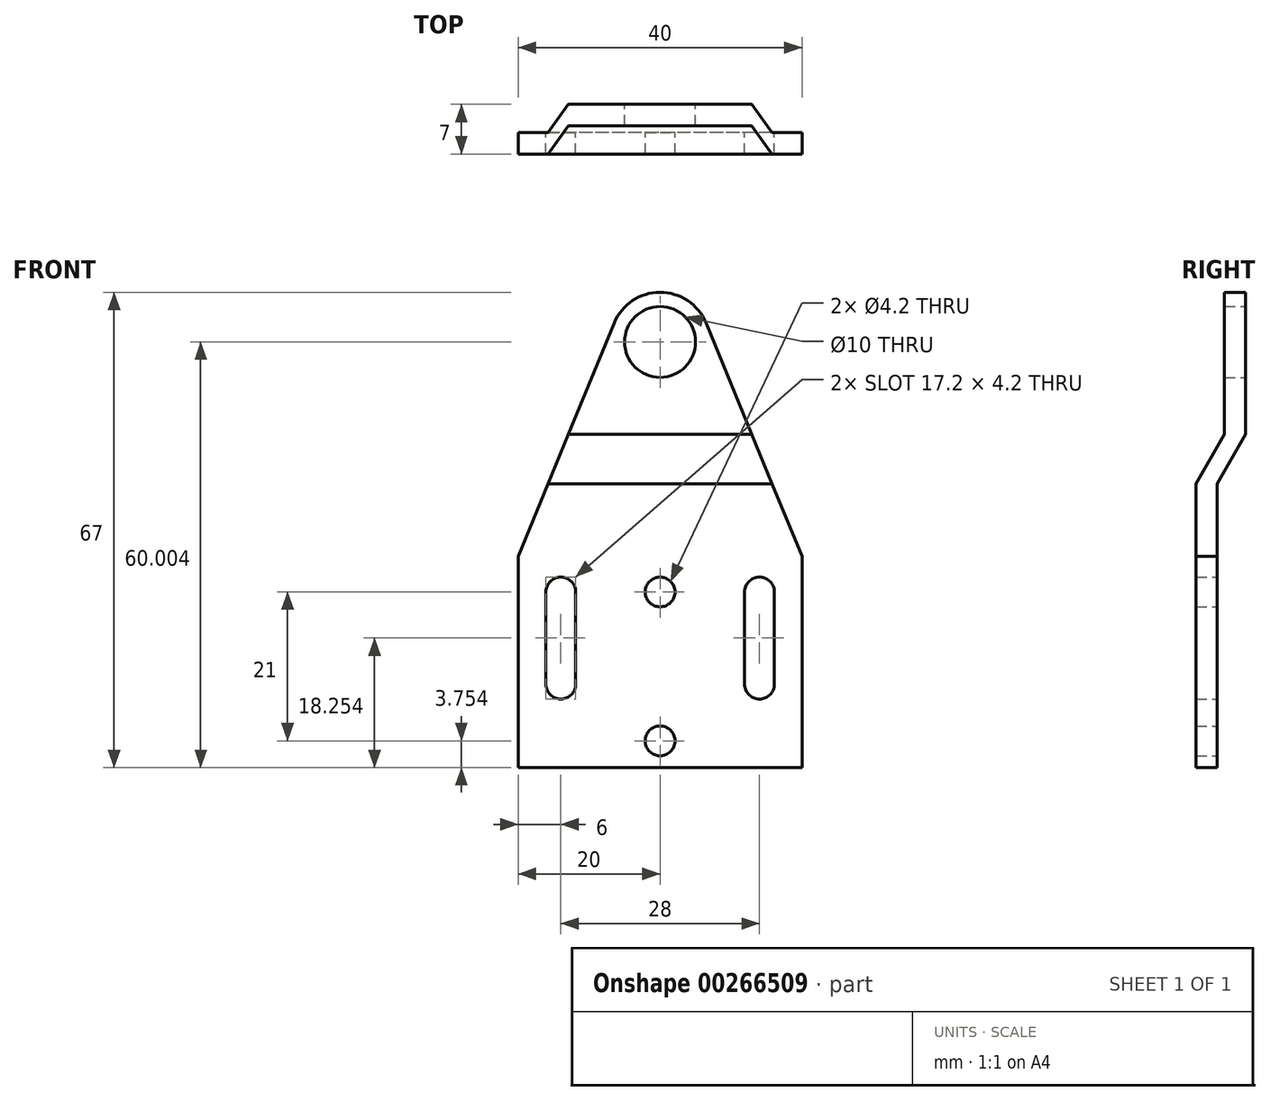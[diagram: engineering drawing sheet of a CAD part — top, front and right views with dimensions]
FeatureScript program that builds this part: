
annotation { "Feature Type Name" : "Feature", "Feature Type Description" : "" }
export const myFeature = defineFeature(function(context is Context, id is Id, definition is map)
    precondition{}
    {
        {
            var Q0;
            Q0=qCreatedBy(makeId("Right.planeOp"),FACE);
            var sketch = newSketch(context, id + "F0", { "sketchPlane" : qUnion([Q0])});
            skLineSegment(sketch, "E0", {"start": v(58.43, 41.65) * mm, "end": v(58.43, 32.15) * mm});
            skLineSegment(sketch, "E1", {"start": v(53.43, 32.15) * mm, "end": v(53.43, 41.65) * mm});
            skArc(sketch, "E2", {"start": v(58.43, 41.65) * mm, "mid": v(55.93, 44.15) * mm, "end": v(53.43, 41.65) * mm});
            skLineSegment(sketch, "E3", {"start": v(77.82, 32.15) * mm, "end": v(39.82, 32.15) * mm, "construction": true});
            skPoint(sketch, "E4.orphan", {"position": v(58.43, 32.15) * mm});
            skLineSegment(sketch, "E5", {"start": v(58.43, 32.15) * mm, "end": v(53.43, 32.15) * mm});
            skSolve(sketch);
        }
        {
            var Q0;
            Q0=makeQuery(id+"F0.imprint","IMPRINT",FACE,{"disambiguationData":[TD([[makeQuery(id+"F0.imprint","IMPRINT",EDGE,{"derivedFrom":sQuery(id+"F0.wireOp",EDGE,"E0")}),-1.0]])]});
            var Q1;
            Q1=sQuery(id+"F0.wireOp",EDGE,"E3");
            revolve(context, id + "F1", {"entities" : qUnion([Q0]), "axis" : qUnion([Q1]), "revolveType" : RevolveType.FULL});
        }
        {
            var Q0;
            Q0=makeQuery(id+"F1.opRevolve","SWEPT_FACE",FACE,{"disambiguationData":[OSD([sQuery(id+"F0.wireOp",EDGE,"E1")])]});
            var sketch = newSketch(context, id + "F2", { "sketchPlane" : qUnion([Q0])});
            skCircle(sketch, "E6", {"center": v(0, 32.15) * mm, "radius": 5 * mm});
            skSolve(sketch);
        }
        {
            var Q0;
            Q0=makeQuery(id+"F2.imprint","IMPRINT",FACE,{"disambiguationData":[TD([[makeQuery(id+"F2.imprint","IMPRINT",EDGE,{"derivedFrom":sQuery(id+"F2.wireOp",EDGE,"E6")}),1.0]])]});
            var Q1;
            Q1=sQuery(id+"F2.wireOp",EDGE,"E6");
            extrude(context, id + "F3", {"entities" : qUnion([Q0]), "operationType" : NewBodyOperationType.ADD, "surfaceEntities" : qUnion([Q1]), "depth" : 10 * mm});
        }
        {
            var Q0;
            Q0=makeQuery(id+"F3.opExtrude","CAP_FACE",FACE,{"disambiguationData":[OSD([sQuery(id+"F2.wireOp",EDGE,"E6")])],"isStart":false});
            var sketch = newSketch(context, id + "F4", { "sketchPlane" : qUnion([Q0])});
            skLineSegment(sketch, "E7", {"start": v(0, 32.15) * mm, "end": v(0, -27.85) * mm, "construction": true});
            skPoint(sketch, "E8", {"position": v(-20, 1.9) * mm});
            skArc(sketch, "E9", {"start": v(6.47, 34.81) * mm, "mid": v(0, 39.15) * mm, "end": v(-6.47, 34.81) * mm});
            skLineSegment(sketch, "E10", {"start": v(-20, 1.9) * mm, "end": v(-6.47, 34.81) * mm});
            skLineSegment(sketch, "E11.MirrorCS", {"start": v(20, 1.9) * mm, "end": v(6.47, 34.81) * mm});
            skLineSegment(sketch, "E12", {"start": v(-20, 1.9) * mm, "end": v(-20, -27.85) * mm});
            skLineSegment(sketch, "E13", {"start": v(-20, -27.85) * mm, "end": v(20, -27.85) * mm});
            skLineSegment(sketch, "E14", {"start": v(20, -27.85) * mm, "end": v(20, 1.9) * mm});
            skArc(sketch, "E15", {"start": v(-11.9, -3.1) * mm, "mid": v(-14, -1) * mm, "end": v(-16.1, -3.1) * mm});
            skArc(sketch, "E16", {"start": v(11.9, -16.1) * mm, "mid": v(14, -18.2) * mm, "end": v(16.1, -16.1) * mm});
            skCircle(sketch, "E17", {"center": v(0, -3.1) * mm, "radius": 2.1 * mm});
            skCircle(sketch, "E18", {"center": v(0, -24.1) * mm, "radius": 2.1 * mm});
            skArc(sketch, "E19", {"start": v(16.1, -3.1) * mm, "mid": v(14, -1) * mm, "end": v(11.9, -3.1) * mm});
            skLineSegment(sketch, "E20", {"start": v(-20, -3.1) * mm, "end": v(27.51, -3.1) * mm, "construction": true});
            skArc(sketch, "E21", {"start": v(-16.1, -16.1) * mm, "mid": v(-14, -18.2) * mm, "end": v(-11.9, -16.1) * mm});
            skLineSegment(sketch, "E22", {"start": v(-14, -3.1) * mm, "end": v(-14, -42.55) * mm, "construction": true});
            skLineSegment(sketch, "E23", {"start": v(-11.9, -3.1) * mm, "end": v(-11.9, -16.1) * mm});
            skLineSegment(sketch, "E24", {"start": v(-16.1, -3.1) * mm, "end": v(-16.1, -16.1) * mm});
            skLineSegment(sketch, "E25", {"start": v(11.9, -3.1) * mm, "end": v(11.9, -16.1) * mm});
            skLineSegment(sketch, "E26", {"start": v(16.1, -16.1) * mm, "end": v(16.1, -3.1) * mm});
            skSolve(sketch);
        }
        {
            var Q0;
            Q0=makeQuery(id+"F4.imprint","IMPRINT",FACE,{"disambiguationData":[TD([[makeQuery(id+"F4.imprint","IMPRINT",EDGE,{"derivedFrom":sQuery(id+"F4.wireOp",EDGE,"E9")}),1.0]])]});
            extrude(context, id + "F5", {"entities" : qUnion([Q0]), "depth" : 30 * mm, "hasSecondDirection" : true, "secondDirectionOppositeDirection" : true, "secondDirectionDepth" : 3 * mm});
        }
        {
            var Q0;
            Q0=makeQuery(id+"F5.opExtrude","SWEPT_FACE",FACE,{"disambiguationData":[OSD([sQuery(id+"F4.wireOp",EDGE,"E12")])]});
            var sketch = newSketch(context, id + "F6", { "sketchPlane" : qUnion([Q0])});
            skLineSegment(sketch, "E27", {"start": v(-42.43, 12.15) * mm, "end": v(-42.43, -53.35) * mm});
            skLineSegment(sketch, "E28", {"start": v(-39.43, -53.35) * mm, "end": v(-39.43, 12.15) * mm});
            skLineSegment(sketch, "E29", {"start": v(-42.43, 12.15) * mm, "end": v(-46.43, 19.15) * mm});
            skLineSegment(sketch, "E30", {"start": v(-46.43, 19.15) * mm, "end": v(-46.43, 39.15) * mm});
            skLineSegment(sketch, "E31", {"start": v(-46.43, 19.15) * mm, "end": v(-21.89, 19.15) * mm, "construction": true});
            skLineSegment(sketch, "E32", {"start": v(-39.43, 12.15) * mm, "end": v(-43.43, 19.15) * mm});
            skLineSegment(sketch, "E33", {"start": v(-43.43, 19.15) * mm, "end": v(-43.43, 39.15) * mm});
            skLineSegment(sketch, "E34", {"start": v(-46.43, 39.15) * mm, "end": v(-43.43, 39.15) * mm});
            skLineSegment(sketch, "E35", {"start": v(-42.43, -53.35) * mm, "end": v(-39.43, -53.35) * mm});
            skLineSegment(sketch, "E36", {"start": v(-60.48, 66.84) * mm, "end": v(-1, 66.84) * mm, "construction": true});
            skSolve(sketch);
        }
        {
            var Q0;
            Q0=qSketchRegion(id+"F6",true);
            extrude(context, id + "F7", {"entities" : qUnion([Q0]), "operationType" : NewBodyOperationType.INTERSECT, "endBound" : BoundingType.THROUGH_ALL, "oppositeDirection" : true, "depth" : 25 * mm});
        }
    });
